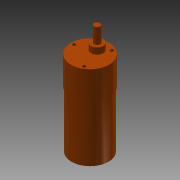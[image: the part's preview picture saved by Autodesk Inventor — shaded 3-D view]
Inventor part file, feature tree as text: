
AUTODESK INVENTOR PART (.ipt)
format: ipt  version: 2013 (Build 170138000, 138)  size: 118,272 bytes
history: native  units: mm
features: sketch x6, extrude x5, thread x3, other x1, hole x1
ambient origin geometry x8: Origin, YZ Plane, XZ Plane, XY Plane, X Axis, Y Axis, Z Axis, Center Point
feature tree (16):
  other  "ソリッド1"
  extrude  "押し出し1"  Depth=35.8mm
  extrude  "押し出し2"  Depth=54.5mm TaperAngle=0.0deg
  extrude  "押し出し3"  Depth=37.0mm
  extrude  "押し出し4"  Depth=27.5mm TaperAngle=0.0deg
  extrude  "押し出し5"  Depth=7.0mm
  hole  "穴1"  [1 undecoded]
  thread  "ねじ1"
  thread  "ねじ2"
  thread  "ねじ3"
  sketch  "スケッチ1"
  sketch  "スケッチ2"
  sketch  "スケッチ3"
  sketch  "スケッチ4"
  sketch  "スケッチ5"
  sketch  "スケッチ6"
note: 1 required parameter value undecoded (feature->parameter linkage not recoverable at this tier; creation-order binding heuristic only, values carry confidence <= 0.55)
